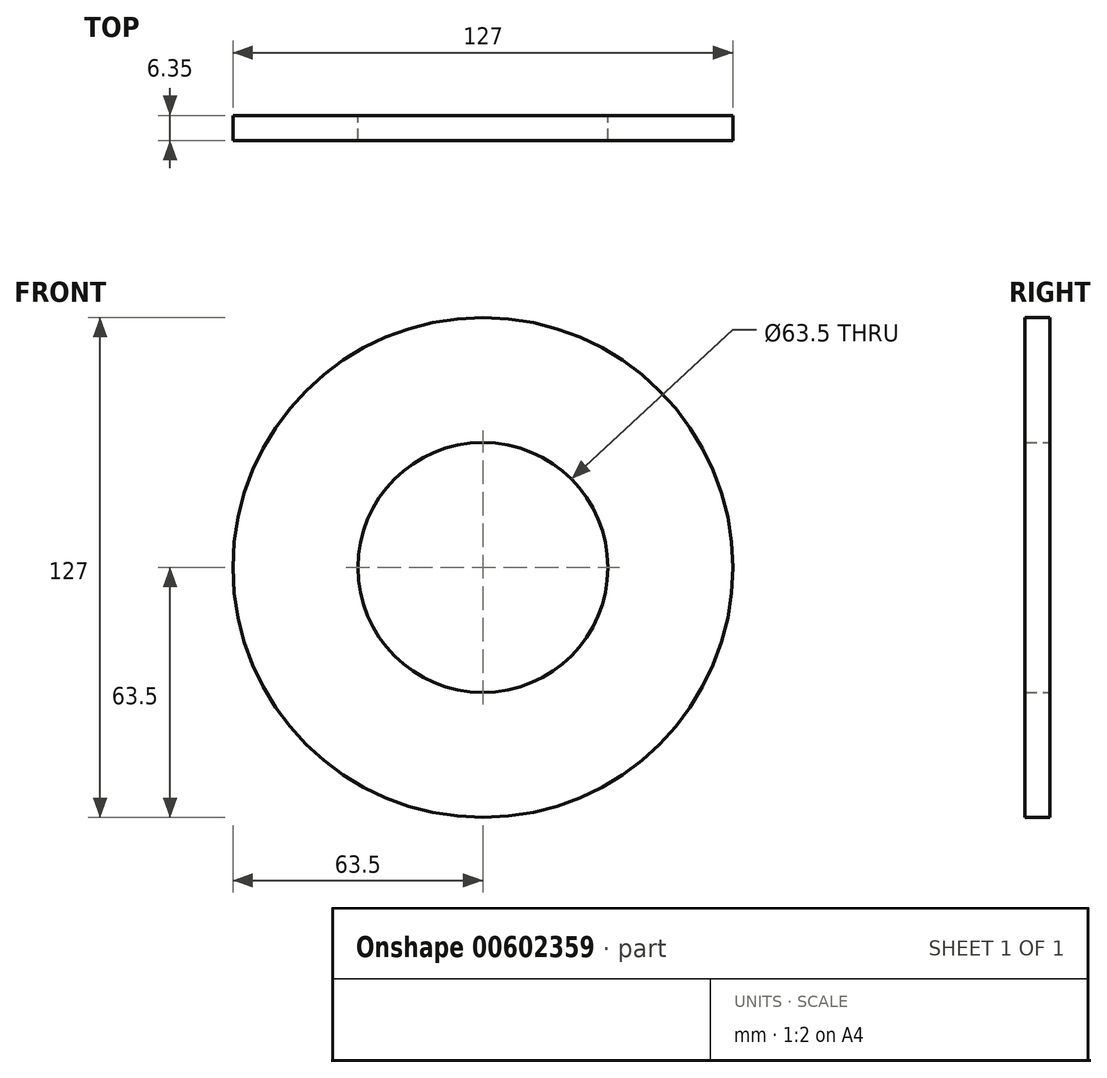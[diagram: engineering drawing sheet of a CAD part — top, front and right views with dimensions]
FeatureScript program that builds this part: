
annotation { "Feature Type Name" : "Feature", "Feature Type Description" : "" }
export const myFeature = defineFeature(function(context is Context, id is Id, definition is map)
    precondition{}
    {
        {
            var Q0;
            Q0=qCreatedBy(makeId("Front.planeOp"),FACE);
            var sketch = newSketch(context, id + "F0", { "sketchPlane" : qUnion([Q0])});
            skCircle(sketch, "E0", {"center": v(0, 0) * mm, "radius": 63.5 * mm});
            skCircle(sketch, "E1", {"center": v(0, 0) * mm, "radius": 31.75 * mm});
            skSolve(sketch);
        }
        {
            var Q0;
            Q0=makeQuery(id+"F0.imprint","IMPRINT",FACE,{"disambiguationData":[TD([[makeQuery(id+"F0.imprint","IMPRINT",EDGE,{"derivedFrom":sQuery(id+"F0.wireOp",EDGE,"E0")}),1.0]])]});
            extrude(context, id + "F1", {"entities" : qUnion([Q0]), "depth" : 6.35 * mm, "offsetDistance" : 25.4 * mm});
        }
    });
